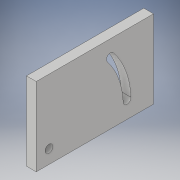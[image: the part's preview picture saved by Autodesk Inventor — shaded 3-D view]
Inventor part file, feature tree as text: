
AUTODESK INVENTOR PART (.ipt)
format: ipt  version: 2019 (Build 230136000, 136)  size: 117,248 bytes
history: native  units: in
note: dims shown in document units (in); Inventor stores cm internally (conversion verified against a paired STEP export)
features: sketch x3, extrude x2, hole x1, projected_geometry x1
ambient origin geometry x8: Origin, YZ Plane, XZ Plane, XY Plane, X Axis, Y Axis, Z Axis, Center Point
bodies: Solid1 (feature_tree)
feature tree (7):
  extrude  "Extrusion1"  Depth=2.0in
  extrude  "Extrusion2"  Depth=0.25in
  hole  "Hole1"  [1 undecoded]
  sketch  "Sketch1"  dims[d0=3.0in d1=2.0in]
  sketch  "Sketch2"  dims[d2=0.25in d3=0.0in d4=0.35in]
  sketch  "Sketch3"  dims[d5=2.0in d6=0.2in d7=0.2in d8=0.25in d9=0.0in d10=0.076in d11=0.198in d12=0.375in d13=0.25in d14=0.5635in d15=0.302in d16=0.8108in]
  projected_geometry  "Projected Loop1"
note: 1 required parameter value undecoded (feature->parameter linkage not recoverable at this tier; creation-order binding heuristic only, values carry confidence <= 0.55)
